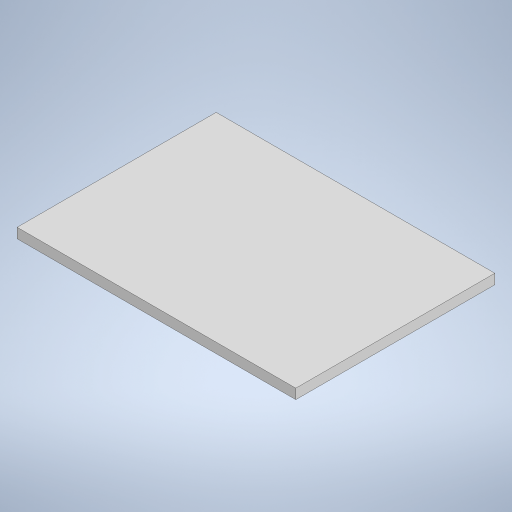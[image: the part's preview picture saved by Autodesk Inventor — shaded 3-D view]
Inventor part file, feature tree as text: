
AUTODESK INVENTOR PART (.ipt)
format: ipt  version: 2024 (Build 280153000, 153)  size: 237,056 bytes
history: native  units: mm
features: extrude x1, sketch x1
ambient origin geometry x8: Origin, YZ Plane, XZ Plane, XY Plane, X Axis, Y Axis, Z Axis, Center Point
bodies: Solid1 (feature_tree)
feature tree (2):
  extrude  "Extrusion1"  Depth=100.0mm
  sketch  "Sketch1"  dims[d0=140.0mm d1=100.0mm d2=5.0mm d3=0.0mm]
